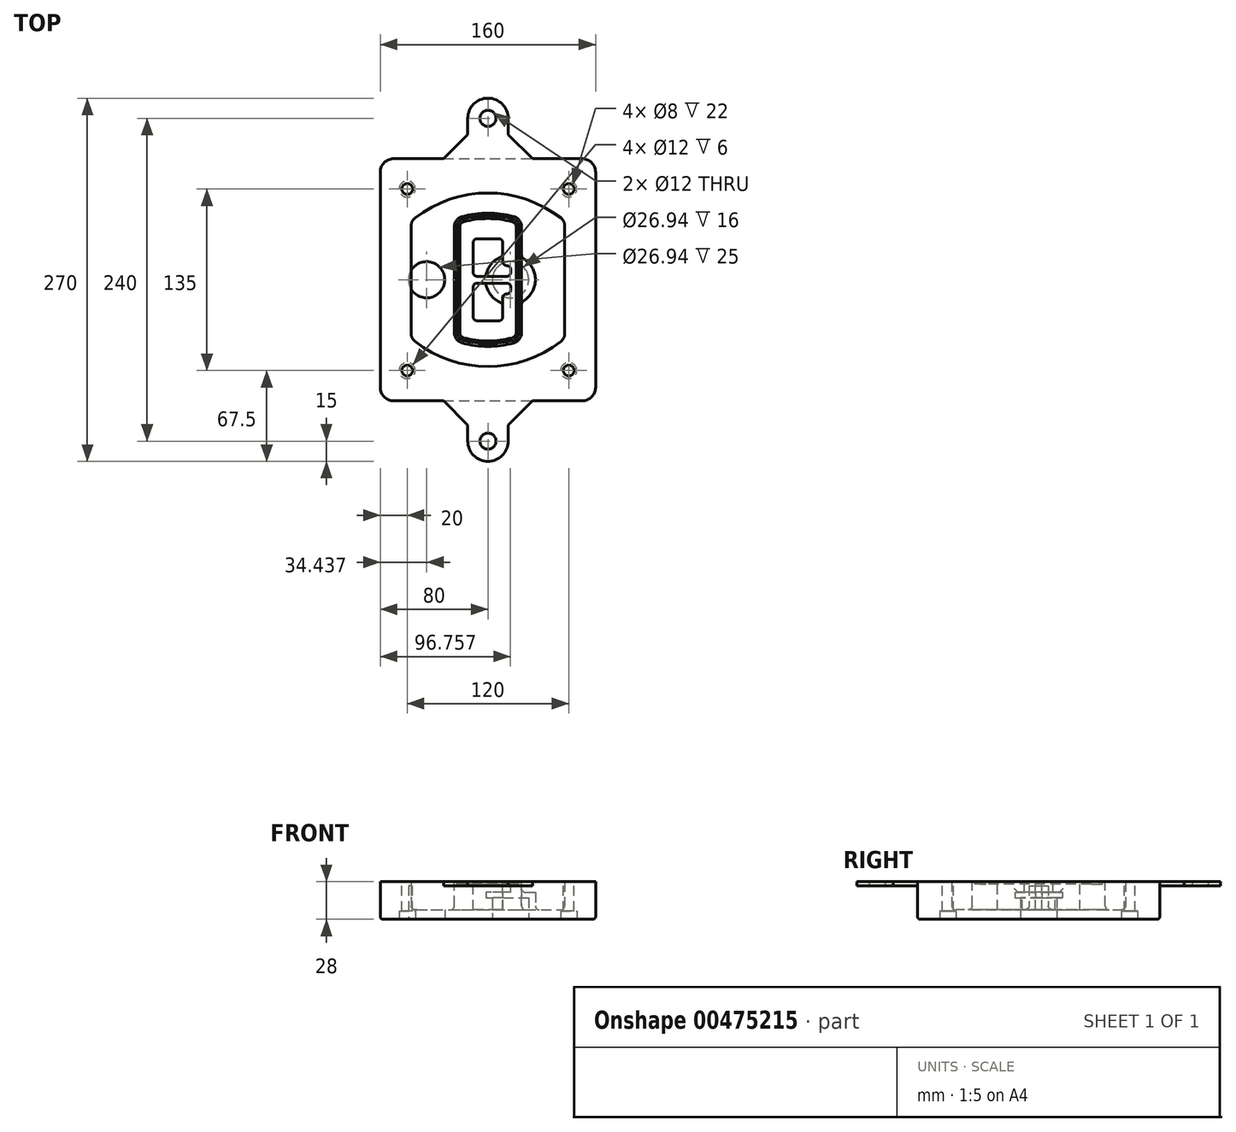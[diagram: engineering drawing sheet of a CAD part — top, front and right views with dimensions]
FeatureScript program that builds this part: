
annotation { "Feature Type Name" : "Feature", "Feature Type Description" : "" }
export const myFeature = defineFeature(function(context is Context, id is Id, definition is map)
    precondition{}
    {
        {
            var Q0;
            Q0=qCreatedBy(makeId("Top.planeOp"),FACE);
            var sketch = newSketch(context, id + "F0", { "sketchPlane" : qUnion([Q0])});
            skPoint(sketch, "E0.rect.middle", {"position": v(0, 0) * mm});
            skLineSegment(sketch, "E1.bottom", {"start": v(-70, -90) * mm, "end": v(70, -90) * mm});
            skLineSegment(sketch, "E1.top", {"start": v(-70, 90) * mm, "end": v(70, 90) * mm});
            skLineSegment(sketch, "E1.left", {"start": v(-80, -80) * mm, "end": v(-80, 80) * mm});
            skLineSegment(sketch, "E1.right", {"start": v(80, -80) * mm, "end": v(80, 80) * mm});
            skLineSegment(sketch, "E2", {"start": v(-80, 90) * mm, "end": v(80, -90) * mm, "construction": true});
            skLineSegment(sketch, "E3", {"start": v(80, 90) * mm, "end": v(-80, -90) * mm, "construction": true});
            skCircle(sketch, "E4", {"center": v(-60, 67.5) * mm, "radius": 4 * mm});
            skCircle(sketch, "E5", {"center": v(60, 67.5) * mm, "radius": 4 * mm});
            skCircle(sketch, "E6", {"center": v(60, -67.5) * mm, "radius": 4 * mm});
            skCircle(sketch, "E7", {"center": v(-60, -67.5) * mm, "radius": 4 * mm});
            skLineSegment(sketch, "E8", {"start": v(-60, 67.5) * mm, "end": v(60, 67.5) * mm, "construction": true});
            skLineSegment(sketch, "E9", {"start": v(60, 67.5) * mm, "end": v(60, -67.5) * mm, "construction": true});
            skLineSegment(sketch, "E10", {"start": v(60, -67.5) * mm, "end": v(-60, -67.5) * mm, "construction": true});
            skLineSegment(sketch, "E11", {"start": v(-60, -67.5) * mm, "end": v(-60, 67.5) * mm, "construction": true});
            skLineSegment(sketch, "E12", {"start": v(-60, 40.3) * mm, "end": v(-60, -40.3) * mm});
            skLineSegment(sketch, "E13", {"start": v(60, 40.3) * mm, "end": v(60, -40.3) * mm});
            skArc(sketch, "E14", {"start": v(56.15, 48.18) * mm, "mid": v(0, 67.5) * mm, "end": v(-56.15, 48.18) * mm});
            skArc(sketch, "E15", {"start": v(-56.15, -48.18) * mm, "mid": v(0, -67.5) * mm, "end": v(56.15, -48.18) * mm});
            skLineSegment(sketch, "E16", {"start": v(-60, 0) * mm, "end": v(60, 0) * mm, "construction": true});
            skPoint(sketch, "E17.visualSharp", {"position": v(-60, -45) * mm});
            skArc(sketch, "E17.filletArc", {"start": v(-60, -40.3) * mm, "mid": v(-58.99, -44.68) * mm, "end": v(-56.15, -48.18) * mm});
            skPoint(sketch, "E18.visualSharp", {"position": v(-60, 45) * mm});
            skArc(sketch, "E18.filletArc", {"start": v(-56.15, 48.18) * mm, "mid": v(-58.99, 44.68) * mm, "end": v(-60, 40.3) * mm});
            skPoint(sketch, "E19.visualSharp", {"position": v(60, 45) * mm});
            skArc(sketch, "E19.filletArc", {"start": v(60, 40.3) * mm, "mid": v(58.99, 44.68) * mm, "end": v(56.15, 48.18) * mm});
            skPoint(sketch, "E20.visualSharp", {"position": v(60, -45) * mm});
            skArc(sketch, "E20.filletArc", {"start": v(56.15, -48.18) * mm, "mid": v(58.99, -44.68) * mm, "end": v(60, -40.3) * mm});
            skPoint(sketch, "E21.visualSharp", {"position": v(-80, 90) * mm});
            skArc(sketch, "E21.filletArc", {"start": v(-70, 90) * mm, "mid": v(-77.07, 87.07) * mm, "end": v(-80, 80) * mm});
            skPoint(sketch, "E22.visualSharp", {"position": v(80, 90) * mm});
            skArc(sketch, "E22.filletArc", {"start": v(80, 80) * mm, "mid": v(77.07, 87.07) * mm, "end": v(70, 90) * mm});
            skPoint(sketch, "E23.visualSharp", {"position": v(80, -90) * mm});
            skArc(sketch, "E23.filletArc", {"start": v(70, -90) * mm, "mid": v(77.07, -87.07) * mm, "end": v(80, -80) * mm});
            skPoint(sketch, "E24.visualSharp", {"position": v(-80, -90) * mm});
            skArc(sketch, "E24.filletArc", {"start": v(-80, -80) * mm, "mid": v(-77.07, -87.07) * mm, "end": v(-70, -90) * mm});
            skArc(sketch, "E25.0", {"start": v(57, 40.3) * mm, "mid": v(56.3, 43.36) * mm, "end": v(54.3, 45.81) * mm});
            skLineSegment(sketch, "E25.1", {"start": v(57, 40.3) * mm, "end": v(57, -40.3) * mm});
            skArc(sketch, "E25.2", {"start": v(54.3, -45.81) * mm, "mid": v(56.3, -43.36) * mm, "end": v(57, -40.3) * mm});
            skArc(sketch, "E25.3", {"start": v(-54.3, -45.81) * mm, "mid": v(0, -64.5) * mm, "end": v(54.3, -45.81) * mm});
            skArc(sketch, "E25.4", {"start": v(-57, -40.3) * mm, "mid": v(-56.3, -43.36) * mm, "end": v(-54.3, -45.81) * mm});
            skArc(sketch, "E25.5", {"start": v(54.3, 45.81) * mm, "mid": v(0, 64.5) * mm, "end": v(-54.3, 45.81) * mm});
            skLineSegment(sketch, "E25.6", {"start": v(-57, 40.3) * mm, "end": v(-57, -40.3) * mm});
            skArc(sketch, "E25.7", {"start": v(-54.3, 45.81) * mm, "mid": v(-56.3, 43.36) * mm, "end": v(-57, 40.3) * mm});
            skArc(sketch, "E26.0", {"start": v(-58.62, 51.33) * mm, "mid": v(-62.58, 46.43) * mm, "end": v(-64, 40.3) * mm});
            skArc(sketch, "E26.1", {"start": v(58.62, 51.33) * mm, "mid": v(0, 71.5) * mm, "end": v(-58.62, 51.33) * mm});
            skArc(sketch, "E26.2", {"start": v(64, 40.3) * mm, "mid": v(62.58, 46.43) * mm, "end": v(58.62, 51.33) * mm});
            skLineSegment(sketch, "E26.3", {"start": v(64, 40.3) * mm, "end": v(64, -40.3) * mm});
            skArc(sketch, "E26.4", {"start": v(58.62, -51.33) * mm, "mid": v(62.58, -46.43) * mm, "end": v(64, -40.3) * mm});
            skLineSegment(sketch, "E26.5", {"start": v(-64, 40.3) * mm, "end": v(-64, -40.3) * mm});
            skArc(sketch, "E26.6", {"start": v(-58.62, -51.33) * mm, "mid": v(0, -71.5) * mm, "end": v(58.62, -51.33) * mm});
            skArc(sketch, "E26.7", {"start": v(-64, -40.3) * mm, "mid": v(-62.58, -46.43) * mm, "end": v(-58.62, -51.33) * mm});
            skSolve(sketch);
        }
        {
            var Q0;
            Q0=makeQuery(id+"F0.imprint","IMPRINT",FACE,{"disambiguationData":[TD([[makeQuery(id+"F0.imprint","IMPRINT",EDGE,{"derivedFrom":sQuery(id+"F0.wireOp",EDGE,"E1.bottom")}),1.0]])]});
            var Q1;
            Q1=makeQuery(id+"F0.imprint","IMPRINT",FACE,{"disambiguationData":[TD([[makeQuery(id+"F0.imprint","IMPRINT",EDGE,{"derivedFrom":sQuery(id+"F0.wireOp",EDGE,"E12")}),1.0]])]});
            var Q2;
            Q2=makeQuery(id+"F0.imprint","IMPRINT",FACE,{"disambiguationData":[TD([[makeQuery(id+"F0.imprint","IMPRINT",EDGE,{"derivedFrom":sQuery(id+"F0.wireOp",EDGE,"E25.0")}),1.0]])]});
            var Q3;
            Q3=makeQuery(id+"F0.imprint","IMPRINT",FACE,{"disambiguationData":[TD([[makeQuery(id+"F0.imprint","IMPRINT",EDGE,{"derivedFrom":sQuery(id+"F0.wireOp",EDGE,"E12")}),-1.0]])]});
            extrude(context, id + "F1", {"entities" : qUnion([Q0, Q1, Q2, Q3]), "oppositeDirection" : true, "depth" : 25 * mm});
        }
        {
            var Q0;
            Q0=makeQuery(id+"F0.imprint","IMPRINT",FACE,{"disambiguationData":[TD([[makeQuery(id+"F0.imprint","IMPRINT",EDGE,{"derivedFrom":sQuery(id+"F0.wireOp",EDGE,"E12")}),1.0]])]});
            extrude(context, id + "F2", {"entities" : qUnion([Q0]), "operationType" : NewBodyOperationType.ADD, "depth" : 3 * mm});
        }
        {
            var Q0;
            Q0=makeQuery(id+"F0.imprint","IMPRINT",FACE,{"disambiguationData":[TD([[makeQuery(id+"F0.imprint","IMPRINT",EDGE,{"derivedFrom":sQuery(id+"F0.wireOp",EDGE,"E25.0")}),1.0]])]});
            extrude(context, id + "F3", {"entities" : qUnion([Q0]), "operationType" : NewBodyOperationType.REMOVE, "oppositeDirection" : true, "depth" : 18 * mm});
        }
        {
            var Q0;
            Q0=makeQuery(id+"F2.opExtrude","CAP_FACE",FACE,{"disambiguationData":[OSD([sQuery(id+"F0.wireOp",EDGE,"E12"),sQuery(id+"F0.wireOp",EDGE,"E13"),sQuery(id+"F0.wireOp",EDGE,"E14"),sQuery(id+"F0.wireOp",EDGE,"E15"),sQuery(id+"F0.wireOp",EDGE,"E17.filletArc"),sQuery(id+"F0.wireOp",EDGE,"E18.filletArc"),sQuery(id+"F0.wireOp",EDGE,"E19.filletArc"),sQuery(id+"F0.wireOp",EDGE,"E20.filletArc"),sQuery(id+"F0.wireOp",EDGE,"E25.0"),sQuery(id+"F0.wireOp",EDGE,"E25.1"),sQuery(id+"F0.wireOp",EDGE,"E25.2"),sQuery(id+"F0.wireOp",EDGE,"E25.3"),sQuery(id+"F0.wireOp",EDGE,"E25.4"),sQuery(id+"F0.wireOp",EDGE,"E25.5"),sQuery(id+"F0.wireOp",EDGE,"E25.6"),sQuery(id+"F0.wireOp",EDGE,"E25.7")])],"isStart":false});
            var sketch = newSketch(context, id + "F4", { "sketchPlane" : qUnion([Q0])});
            skArc(sketch, "E27.0", {"start": v(-19.08, -46.97) * mm, "mid": v(0, -49.5) * mm, "end": v(19.08, -46.97) * mm});
            skArc(sketch, "E28.0", {"start": v(19.08, 46.97) * mm, "mid": v(0, 49.5) * mm, "end": v(-19.08, 46.97) * mm});
            skLineSegment(sketch, "E29", {"start": v(-25, 39.25) * mm, "end": v(-25, -39.25) * mm});
            skLineSegment(sketch, "E30", {"start": v(25, 39.25) * mm, "end": v(25, -39.25) * mm});
            skLineSegment(sketch, "E31", {"start": v(-25, 45.1) * mm, "end": v(25, 45.1) * mm, "construction": true});
            skLineSegment(sketch, "E32", {"start": v(-25, -45.1) * mm, "end": v(25, -45.1) * mm, "construction": true});
            skPoint(sketch, "E33.visualSharp", {"position": v(-25, 45.1) * mm});
            skArc(sketch, "E33.filletArc", {"start": v(-19.08, 46.97) * mm, "mid": v(-23.35, 44.11) * mm, "end": v(-25, 39.25) * mm});
            skPoint(sketch, "E34.visualSharp", {"position": v(25, 45.1) * mm});
            skArc(sketch, "E34.filletArc", {"start": v(25, 39.25) * mm, "mid": v(23.35, 44.11) * mm, "end": v(19.08, 46.97) * mm});
            skPoint(sketch, "E35.visualSharp", {"position": v(25, -45.1) * mm});
            skArc(sketch, "E35.filletArc", {"start": v(19.08, -46.97) * mm, "mid": v(23.35, -44.11) * mm, "end": v(25, -39.25) * mm});
            skPoint(sketch, "E36.visualSharp", {"position": v(-25, -45.1) * mm});
            skArc(sketch, "E36.filletArc", {"start": v(-25, -39.25) * mm, "mid": v(-23.35, -44.11) * mm, "end": v(-19.08, -46.97) * mm});
            skArc(sketch, "E37.0", {"start": v(54.3, 45.81) * mm, "mid": v(0, 64.5) * mm, "end": v(-54.3, 45.81) * mm});
            skArc(sketch, "E37.1", {"start": v(-54.3, 45.81) * mm, "mid": v(-56.3, 43.36) * mm, "end": v(-57, 40.3) * mm});
            skLineSegment(sketch, "E37.2", {"start": v(-57, 40.3) * mm, "end": v(-57, -40.3) * mm});
            skArc(sketch, "E37.3", {"start": v(-57, -40.3) * mm, "mid": v(-56.3, -43.36) * mm, "end": v(-54.3, -45.81) * mm});
            skArc(sketch, "E37.4", {"start": v(-54.3, -45.81) * mm, "mid": v(0, -64.5) * mm, "end": v(54.3, -45.81) * mm});
            skArc(sketch, "E37.5", {"start": v(54.3, -45.81) * mm, "mid": v(56.3, -43.36) * mm, "end": v(57, -40.3) * mm});
            skLineSegment(sketch, "E37.6", {"start": v(57, 40.3) * mm, "end": v(57, -40.3) * mm});
            skArc(sketch, "E37.7", {"start": v(57, 40.3) * mm, "mid": v(56.3, 43.36) * mm, "end": v(54.3, 45.81) * mm});
            skLineSegment(sketch, "E38.0", {"start": v(23, 39.25) * mm, "end": v(23, -39.25) * mm});
            skArc(sketch, "E38.1", {"start": v(18.56, -45.04) * mm, "mid": v(21.76, -42.9) * mm, "end": v(23, -39.25) * mm});
            skArc(sketch, "E38.2", {"start": v(-18.56, -45.04) * mm, "mid": v(0, -47.5) * mm, "end": v(18.56, -45.04) * mm});
            skArc(sketch, "E38.3", {"start": v(-23, -39.25) * mm, "mid": v(-21.76, -42.9) * mm, "end": v(-18.56, -45.04) * mm});
            skLineSegment(sketch, "E38.4", {"start": v(-23, 39.25) * mm, "end": v(-23, -39.25) * mm});
            skArc(sketch, "E38.5", {"start": v(23, 39.25) * mm, "mid": v(21.76, 42.9) * mm, "end": v(18.56, 45.04) * mm});
            skArc(sketch, "E38.6", {"start": v(-18.56, 45.04) * mm, "mid": v(-21.76, 42.9) * mm, "end": v(-23, 39.25) * mm});
            skArc(sketch, "E38.7", {"start": v(18.56, 45.04) * mm, "mid": v(0, 47.5) * mm, "end": v(-18.56, 45.04) * mm});
            skArc(sketch, "E39.0", {"start": v(21, 39.25) * mm, "mid": v(20.18, 41.68) * mm, "end": v(18.04, 43.1) * mm});
            skLineSegment(sketch, "E39.1", {"start": v(21, 39.25) * mm, "end": v(21, -39.25) * mm});
            skArc(sketch, "E39.2", {"start": v(18.04, -43.1) * mm, "mid": v(20.18, -41.68) * mm, "end": v(21, -39.25) * mm});
            skArc(sketch, "E39.3", {"start": v(-18.04, -43.1) * mm, "mid": v(0, -45.5) * mm, "end": v(18.04, -43.1) * mm});
            skArc(sketch, "E39.4", {"start": v(-21, -39.25) * mm, "mid": v(-20.18, -41.68) * mm, "end": v(-18.04, -43.1) * mm});
            skArc(sketch, "E39.5", {"start": v(18.04, 43.1) * mm, "mid": v(0, 45.5) * mm, "end": v(-18.04, 43.1) * mm});
            skLineSegment(sketch, "E39.6", {"start": v(-21, 39.25) * mm, "end": v(-21, -39.25) * mm});
            skArc(sketch, "E39.7", {"start": v(-18.04, 43.1) * mm, "mid": v(-20.18, 41.68) * mm, "end": v(-21, 39.25) * mm});
            skLineSegment(sketch, "E40", {"start": v(-25, 0) * mm, "end": v(25, 0) * mm, "construction": true});
            skLineSegment(sketch, "E41", {"start": v(-11, 5.5) * mm, "end": v(-11, 27.5) * mm});
            skLineSegment(sketch, "E42", {"start": v(-8, 30.5) * mm, "end": v(8, 30.5) * mm});
            skLineSegment(sketch, "E43", {"start": v(11, 27.5) * mm, "end": v(11, 13.5) * mm});
            skLineSegment(sketch, "E44", {"start": v(14, 10.5) * mm, "end": v(14, 10.5) * mm});
            skLineSegment(sketch, "E45", {"start": v(17, 7.5) * mm, "end": v(17, 5.5) * mm});
            skLineSegment(sketch, "E46", {"start": v(14, 2.5) * mm, "end": v(-8, 2.5) * mm});
            skPoint(sketch, "E47.visualSharp", {"position": v(-11, 30.5) * mm});
            skArc(sketch, "E47.filletArc", {"start": v(-8, 30.5) * mm, "mid": v(-10.12, 29.62) * mm, "end": v(-11, 27.5) * mm});
            skPoint(sketch, "E48.visualSharp", {"position": v(11, 30.5) * mm});
            skArc(sketch, "E48.filletArc", {"start": v(11, 27.5) * mm, "mid": v(10.12, 29.62) * mm, "end": v(8, 30.5) * mm});
            skPoint(sketch, "E49.visualSharp", {"position": v(11, 10.5) * mm});
            skArc(sketch, "E49.filletArc", {"start": v(11, 13.5) * mm, "mid": v(11.88, 11.38) * mm, "end": v(14, 10.5) * mm});
            skPoint(sketch, "E50.visualSharp", {"position": v(17, 10.5) * mm});
            skArc(sketch, "E50.filletArc", {"start": v(17, 7.5) * mm, "mid": v(16.12, 9.62) * mm, "end": v(14, 10.5) * mm});
            skPoint(sketch, "E51.visualSharp", {"position": v(17, 2.5) * mm});
            skArc(sketch, "E51.filletArc", {"start": v(14, 2.5) * mm, "mid": v(16.12, 3.38) * mm, "end": v(17, 5.5) * mm});
            skPoint(sketch, "E52.visualSharp", {"position": v(-11, 2.5) * mm});
            skArc(sketch, "E52.filletArc", {"start": v(-11, 5.5) * mm, "mid": v(-10.12, 3.38) * mm, "end": v(-8, 2.5) * mm});
            skLineSegment(sketch, "E53.0.MirrorCS", {"start": v(14, -2.5) * mm, "end": v(-8, -2.5) * mm});
            skArc(sketch, "E54.0.MirrorCS", {"start": v(-11, -5.5) * mm, "mid": v(-10.12, -3.38) * mm, "end": v(-8, -2.5) * mm});
            skLineSegment(sketch, "E55.0.MirrorCS", {"start": v(-11, -5.5) * mm, "end": v(-11, -27.5) * mm});
            skArc(sketch, "E56.0.MirrorCS", {"start": v(-8, -30.5) * mm, "mid": v(-10.12, -29.62) * mm, "end": v(-11, -27.5) * mm});
            skLineSegment(sketch, "E57.0.MirrorCS", {"start": v(-8, -30.5) * mm, "end": v(8, -30.5) * mm});
            skArc(sketch, "E58.0.MirrorCS", {"start": v(11, -27.5) * mm, "mid": v(10.12, -29.62) * mm, "end": v(8, -30.5) * mm});
            skLineSegment(sketch, "E59.0.MirrorCS", {"start": v(11, -27.5) * mm, "end": v(11, -13.5) * mm});
            skArc(sketch, "E60.0.MirrorCS", {"start": v(11, -13.5) * mm, "mid": v(11.88, -11.38) * mm, "end": v(14, -10.5) * mm});
            skArc(sketch, "E61.0.MirrorCS", {"start": v(17, -7.5) * mm, "mid": v(16.12, -9.62) * mm, "end": v(14, -10.5) * mm});
            skLineSegment(sketch, "E62.0.MirrorCS", {"start": v(17, -7.5) * mm, "end": v(17, -5.5) * mm});
            skArc(sketch, "E63.0.MirrorCS", {"start": v(14, -2.5) * mm, "mid": v(16.12, -3.38) * mm, "end": v(17, -5.5) * mm});
            skSolve(sketch);
        }
        {
            var Q0;
            Q0=makeQuery(id+"F4.imprint","IMPRINT",FACE,{"disambiguationData":[TD([[makeQuery(id+"F4.imprint","IMPRINT",EDGE,{"derivedFrom":sQuery(id+"F4.wireOp",EDGE,"E27.0")}),1.0]])]});
            var Q1;
            Q1=makeQuery(id+"F4.imprint","IMPRINT",FACE,{"disambiguationData":[TD([[makeQuery(id+"F4.imprint","IMPRINT",EDGE,{"derivedFrom":sQuery(id+"F4.wireOp",EDGE,"E38.0")}),-1.0]])]});
            var Q2;
            Q2=makeQuery(id+"F4.imprint","IMPRINT",FACE,{"disambiguationData":[TD([[makeQuery(id+"F4.imprint","IMPRINT",EDGE,{"derivedFrom":sQuery(id+"F4.wireOp",EDGE,"E39.0")}),1.0]])]});
            extrude(context, id + "F5", {"entities" : qUnion([Q0, Q1, Q2]), "operationType" : NewBodyOperationType.ADD, "endBound" : BoundingType.UP_TO_NEXT, "oppositeDirection" : true, "depth" : 25 * mm});
        }
        {
            var Q0;
            Q0=makeQuery(id+"F4.imprint","IMPRINT",FACE,{"disambiguationData":[TD([[makeQuery(id+"F4.imprint","IMPRINT",EDGE,{"derivedFrom":sQuery(id+"F4.wireOp",EDGE,"E38.0")}),-1.0]])]});
            extrude(context, id + "F6", {"entities" : qUnion([Q0]), "operationType" : NewBodyOperationType.REMOVE, "oppositeDirection" : true, "depth" : 2 * mm});
        }
        {
            var Q0;
            Q0=makeQuery(id+"F1.opExtrude","CAP_FACE",FACE,{"disambiguationData":[OSD([sQuery(id+"F0.wireOp",EDGE,"E1.bottom"),sQuery(id+"F0.wireOp",EDGE,"E1.top"),sQuery(id+"F0.wireOp",EDGE,"E1.left"),sQuery(id+"F0.wireOp",EDGE,"E1.right"),sQuery(id+"F0.wireOp",EDGE,"E4"),sQuery(id+"F0.wireOp",EDGE,"E5"),sQuery(id+"F0.wireOp",EDGE,"E6"),sQuery(id+"F0.wireOp",EDGE,"E7"),sQuery(id+"F0.wireOp",EDGE,"E21.filletArc"),sQuery(id+"F0.wireOp",EDGE,"E22.filletArc"),sQuery(id+"F0.wireOp",EDGE,"E23.filletArc"),sQuery(id+"F0.wireOp",EDGE,"E24.filletArc")])],"isStart":false});
            var sketch = newSketch(context, id + "F7", { "sketchPlane" : qUnion([Q0])});
            skCircle(sketch, "E64", {"center": v(16.76, 0) * mm, "radius": 13.47 * mm});
            skCircle(sketch, "E65", {"center": v(-45.56, 0) * mm, "radius": 13.47 * mm});
            skLineSegment(sketch, "E66", {"start": v(80, 0) * mm, "end": v(-80, 0) * mm});
            skCircle(sketch, "E67", {"center": v(16.76, 0) * mm, "radius": 18.47 * mm});
            skCircle(sketch, "E68", {"center": v(60, -67.5) * mm, "radius": 6 * mm});
            skCircle(sketch, "E69", {"center": v(-60, -67.5) * mm, "radius": 6 * mm});
            skCircle(sketch, "E70", {"center": v(-60, 67.5) * mm, "radius": 6 * mm});
            skCircle(sketch, "E71", {"center": v(60, 67.5) * mm, "radius": 6 * mm});
            skSolve(sketch);
        }
        {
            var Q0;
            {var subQ1=sQuery(id+"F7.wireOp",EDGE,"E66");var subQ4=sQuery(id+"F7.wireOp",EDGE,"E64");var subQ6=makeQuery(id+"F7.imprint","INTERSECT",VERTEX,{"disambiguationData":[OD(0.0)],"derivedFrom":[subQ4,subQ1]});Q0=makeQuery(id+"F7.imprint","IMPRINT",FACE,{"disambiguationData":[TD([[makeQuery(id+"F7.imprint","IMPRINT",EDGE,{"disambiguationData":[TD([[subQ6,-1.0]])],"derivedFrom":subQ4}),-1.0]])]});}
            var Q1;
            {var subQ0=sQuery(id+"F7.wireOp",EDGE,"E66");var subQ1=sQuery(id+"F7.wireOp",EDGE,"E64");var subQ3=makeQuery(id+"F7.imprint","INTERSECT",VERTEX,{"disambiguationData":[OD(0.0)],"derivedFrom":[subQ1,subQ0]});Q1=makeQuery(id+"F7.imprint","IMPRINT",FACE,{"disambiguationData":[TD([[makeQuery(id+"F7.imprint","IMPRINT",EDGE,{"disambiguationData":[TD([[subQ3,-1.0]])],"derivedFrom":subQ1}),1.0]])]});}
            var Q2;
            {var subQ0=sQuery(id+"F7.wireOp",EDGE,"E66");var subQ1=sQuery(id+"F7.wireOp",EDGE,"E64");var subQ3=makeQuery(id+"F7.imprint","INTERSECT",VERTEX,{"disambiguationData":[OD(0.0)],"derivedFrom":[subQ1,subQ0]});Q2=makeQuery(id+"F7.imprint","IMPRINT",FACE,{"disambiguationData":[TD([[makeQuery(id+"F7.imprint","IMPRINT",EDGE,{"disambiguationData":[TD([[subQ3,1.0]])],"derivedFrom":subQ1}),1.0]])]});}
            var Q3;
            {var subQ1=sQuery(id+"F7.wireOp",EDGE,"E66");var subQ4=sQuery(id+"F7.wireOp",EDGE,"E64");var subQ6=makeQuery(id+"F7.imprint","INTERSECT",VERTEX,{"disambiguationData":[OD(0.0)],"derivedFrom":[subQ4,subQ1]});Q3=makeQuery(id+"F7.imprint","IMPRINT",FACE,{"disambiguationData":[TD([[makeQuery(id+"F7.imprint","IMPRINT",EDGE,{"disambiguationData":[TD([[subQ6,1.0]])],"derivedFrom":subQ4}),-1.0]])]});}
            extrude(context, id + "F8", {"entities" : qUnion([Q0, Q1, Q2, Q3]), "operationType" : NewBodyOperationType.ADD, "oppositeDirection" : true, "depth" : 20 * mm});
        }
        {
            var Q0;
            {var subQ0=sQuery(id+"F7.wireOp",EDGE,"E66");var subQ1=sQuery(id+"F7.wireOp",EDGE,"E64");var subQ3=makeQuery(id+"F7.imprint","INTERSECT",VERTEX,{"disambiguationData":[OD(0.0)],"derivedFrom":[subQ1,subQ0]});Q0=makeQuery(id+"F7.imprint","IMPRINT",FACE,{"disambiguationData":[TD([[makeQuery(id+"F7.imprint","IMPRINT",EDGE,{"disambiguationData":[TD([[subQ3,-1.0]])],"derivedFrom":subQ1}),1.0]])]});}
            var Q1;
            {var subQ0=sQuery(id+"F7.wireOp",EDGE,"E66");var subQ1=sQuery(id+"F7.wireOp",EDGE,"E64");var subQ3=makeQuery(id+"F7.imprint","INTERSECT",VERTEX,{"disambiguationData":[OD(0.0)],"derivedFrom":[subQ1,subQ0]});Q1=makeQuery(id+"F7.imprint","IMPRINT",FACE,{"disambiguationData":[TD([[makeQuery(id+"F7.imprint","IMPRINT",EDGE,{"disambiguationData":[TD([[subQ3,1.0]])],"derivedFrom":subQ1}),1.0]])]});}
            extrude(context, id + "F9", {"entities" : qUnion([Q0, Q1]), "operationType" : NewBodyOperationType.REMOVE, "oppositeDirection" : true, "depth" : 16 * mm});
        }
        {
            var Q0;
            {var subQ0=sQuery(id+"F7.wireOp",EDGE,"E66");var subQ1=sQuery(id+"F7.wireOp",EDGE,"E65");var subQ3=makeQuery(id+"F7.imprint","INTERSECT",VERTEX,{"disambiguationData":[OD(0.0)],"derivedFrom":[subQ1,subQ0]});Q0=makeQuery(id+"F7.imprint","IMPRINT",FACE,{"disambiguationData":[TD([[makeQuery(id+"F7.imprint","IMPRINT",EDGE,{"disambiguationData":[TD([[subQ3,-1.0]])],"derivedFrom":subQ1}),1.0]])]});}
            var Q1;
            {var subQ0=sQuery(id+"F7.wireOp",EDGE,"E66");var subQ1=sQuery(id+"F7.wireOp",EDGE,"E65");var subQ3=makeQuery(id+"F7.imprint","INTERSECT",VERTEX,{"disambiguationData":[OD(0.0)],"derivedFrom":[subQ1,subQ0]});Q1=makeQuery(id+"F7.imprint","IMPRINT",FACE,{"disambiguationData":[TD([[makeQuery(id+"F7.imprint","IMPRINT",EDGE,{"disambiguationData":[TD([[subQ3,1.0]])],"derivedFrom":subQ1}),1.0]])]});}
            extrude(context, id + "F10", {"entities" : qUnion([Q0, Q1]), "operationType" : NewBodyOperationType.REMOVE, "oppositeDirection" : true, "depth" : 25 * mm});
        }
        {
            var Q0;
            Q0=makeQuery(id+"F7.imprint","IMPRINT",FACE,{"disambiguationData":[TD([[makeQuery(id+"F7.imprint","IMPRINT",EDGE,{"derivedFrom":sQuery(id+"F7.wireOp",EDGE,"E68")}),1.0]])]});
            var Q1;
            Q1=makeQuery(id+"F7.imprint","IMPRINT",FACE,{"disambiguationData":[TD([[makeQuery(id+"F7.imprint","IMPRINT",EDGE,{"derivedFrom":makeQuery(id+"F1.opExtrude","CAP_EDGE",EDGE,{"disambiguationData":[OSD([sQuery(id+"F0.wireOp",EDGE,"E5")])],"isStart":false})}),-1.0]])]});
            var Q2;
            Q2=makeQuery(id+"F7.imprint","IMPRINT",FACE,{"disambiguationData":[TD([[makeQuery(id+"F7.imprint","IMPRINT",EDGE,{"derivedFrom":sQuery(id+"F7.wireOp",EDGE,"E69")}),1.0]])]});
            var Q3;
            Q3=makeQuery(id+"F7.imprint","IMPRINT",FACE,{"disambiguationData":[TD([[makeQuery(id+"F7.imprint","IMPRINT",EDGE,{"derivedFrom":makeQuery(id+"F1.opExtrude","CAP_EDGE",EDGE,{"disambiguationData":[OSD([sQuery(id+"F0.wireOp",EDGE,"E4")])],"isStart":false})}),-1.0]])]});
            var Q4;
            Q4=makeQuery(id+"F7.imprint","IMPRINT",FACE,{"disambiguationData":[TD([[makeQuery(id+"F7.imprint","IMPRINT",EDGE,{"derivedFrom":sQuery(id+"F7.wireOp",EDGE,"E70")}),1.0]])]});
            var Q5;
            Q5=makeQuery(id+"F7.imprint","IMPRINT",FACE,{"disambiguationData":[TD([[makeQuery(id+"F7.imprint","IMPRINT",EDGE,{"derivedFrom":makeQuery(id+"F1.opExtrude","CAP_EDGE",EDGE,{"disambiguationData":[OSD([sQuery(id+"F0.wireOp",EDGE,"E7")])],"isStart":false})}),-1.0]])]});
            var Q6;
            Q6=makeQuery(id+"F7.imprint","IMPRINT",FACE,{"disambiguationData":[TD([[makeQuery(id+"F7.imprint","IMPRINT",EDGE,{"derivedFrom":sQuery(id+"F7.wireOp",EDGE,"E71")}),1.0]])]});
            var Q7;
            Q7=makeQuery(id+"F7.imprint","IMPRINT",FACE,{"disambiguationData":[TD([[makeQuery(id+"F7.imprint","IMPRINT",EDGE,{"derivedFrom":makeQuery(id+"F1.opExtrude","CAP_EDGE",EDGE,{"disambiguationData":[OSD([sQuery(id+"F0.wireOp",EDGE,"E6")])],"isStart":false})}),-1.0]])]});
            extrude(context, id + "F11", {"entities" : qUnion([Q0, Q1, Q2, Q3, Q4, Q5, Q6, Q7]), "operationType" : NewBodyOperationType.REMOVE, "oppositeDirection" : true, "depth" : 6 * mm});
        }
        {
            var Q0;
            Q0=makeQuery(id+"F9.boolean.opBoolean","COPY",FACE,{"derivedFrom":makeQuery(id+"F9.opExtrude","CAP_FACE",FACE,{"disambiguationData":[OSD([sQuery(id+"F7.wireOp",EDGE,"E64")])],"isStart":false})});
            var sketch = newSketch(context, id + "F12", { "sketchPlane" : qUnion([Q0])});
            skArc(sketch, "E72.0", {"start": v(11, 17.55) * mm, "mid": v(2.57, 11.82) * mm, "end": v(-1.54, 2.5) * mm});
            skArc(sketch, "E72.1", {"start": v(-1.54, -2.5) * mm, "mid": v(2.57, -11.82) * mm, "end": v(11, -17.55) * mm});
            skLineSegment(sketch, "E73", {"start": v(-1.54, -2.5) * mm, "end": v(14, -2.5) * mm});
            skLineSegment(sketch, "E74.0", {"start": v(14, 2.5) * mm, "end": v(-1.54, 2.5) * mm});
            skArc(sketch, "E74.1", {"start": v(14, 2.5) * mm, "mid": v(16.12, 3.38) * mm, "end": v(17, 5.5) * mm});
            skLineSegment(sketch, "E74.2", {"start": v(17, 7.5) * mm, "end": v(17, 5.5) * mm});
            skArc(sketch, "E74.3", {"start": v(17, 7.5) * mm, "mid": v(16.12, 9.62) * mm, "end": v(14, 10.5) * mm});
            skArc(sketch, "E74.4", {"start": v(11, 13.5) * mm, "mid": v(11.88, 11.38) * mm, "end": v(14, 10.5) * mm});
            skLineSegment(sketch, "E74.5", {"start": v(11, 17.55) * mm, "end": v(11, 13.5) * mm});
            skLineSegment(sketch, "E74.7", {"start": v(14, -2.5) * mm, "end": v(-1.54, -2.5) * mm});
            skArc(sketch, "E74.8", {"start": v(14, -2.5) * mm, "mid": v(16.12, -3.38) * mm, "end": v(17, -5.5) * mm});
            skLineSegment(sketch, "E74.9", {"start": v(17, -7.5) * mm, "end": v(17, -5.5) * mm});
            skArc(sketch, "E74.10", {"start": v(17, -7.5) * mm, "mid": v(16.12, -9.62) * mm, "end": v(14, -10.5) * mm});
            skArc(sketch, "E74.11", {"start": v(11, -13.5) * mm, "mid": v(11.88, -11.38) * mm, "end": v(14, -10.5) * mm});
            skLineSegment(sketch, "E74.12", {"start": v(11, -17.55) * mm, "end": v(11, -13.5) * mm});
            skPoint(sketch, "E75.orphan", {"position": v(11, -27.5) * mm});
            skPoint(sketch, "E76.orphan", {"position": v(-8, -2.5) * mm});
            skPoint(sketch, "E77.orphan", {"position": v(-8, 2.5) * mm});
            skPoint(sketch, "E78.orphan", {"position": v(11, 27.5) * mm});
            skSolve(sketch);
        }
        {
            var Q0;
            {var subQ7=sQuery(id+"F12.wireOp",EDGE,"E72.0");var subQ14=sQuery(id+"F12.wireOp",EDGE,"E72.1");var subQ16=sQuery(id+"F12.wireOp",EDGE,"E74.1");var subQ18=sQuery(id+"F12.wireOp",EDGE,"E74.8");Q0=qUnion([makeQuery(id+"F12.imprint","IMPRINT",FACE,{"disambiguationData":[TD([[makeQuery(id+"F12.imprint","IMPRINT",EDGE,{"derivedFrom":subQ7}),1.0]])]}),makeQuery(id+"F12.imprint","IMPRINT",FACE,{"disambiguationData":[TD([[makeQuery(id+"F12.imprint","IMPRINT",EDGE,{"derivedFrom":subQ14}),1.0]])]}),makeQuery(id+"F12.imprint","IMPRINT",FACE,{"disambiguationData":[TD([[makeQuery(id+"F12.imprint","IMPRINT",EDGE,{"derivedFrom":subQ16}),1.0]])]}),makeQuery(id+"F12.imprint","IMPRINT",FACE,{"disambiguationData":[TD([[makeQuery(id+"F12.imprint","IMPRINT",EDGE,{"derivedFrom":subQ18}),-1.0]])]})]);}
            var Q1;
            Q1=makeQuery(id+"F5.boolean.opBoolean","SPLIT",FACE,{"disambiguationData":[TD([makeQuery(id+"F5.opExtrude","SWEPT_FACE",FACE,{"disambiguationData":[OSD([sQuery(id+"F4.wireOp",EDGE,"E41")])]})])],"derivedFrom":makeQuery(id+"F3.boolean.opBoolean","COPY",FACE,{"derivedFrom":makeQuery(id+"F3.opExtrude","CAP_FACE",FACE,{"disambiguationData":[OSD([sQuery(id+"F0.wireOp",EDGE,"E25.0"),sQuery(id+"F0.wireOp",EDGE,"E25.1"),sQuery(id+"F0.wireOp",EDGE,"E25.2"),sQuery(id+"F0.wireOp",EDGE,"E25.3"),sQuery(id+"F0.wireOp",EDGE,"E25.4"),sQuery(id+"F0.wireOp",EDGE,"E25.5"),sQuery(id+"F0.wireOp",EDGE,"E25.6"),sQuery(id+"F0.wireOp",EDGE,"E25.7")])],"isStart":false})})});
            extrude(context, id + "F13", {"entities" : qUnion([Q0]), "operationType" : NewBodyOperationType.REMOVE, "endBound" : BoundingType.UP_TO_SURFACE, "endBoundEntityFace" : qUnion([Q1]), "depth" : 25 * mm});
        }
        {
            var Q0;
            Q0=makeQuery(id+"F3.boolean.opBoolean","COPY",EDGE,{"derivedFrom":makeQuery(id+"F3.opExtrude","CAP_EDGE",EDGE,{"disambiguationData":[OSD([sQuery(id+"F0.wireOp",EDGE,"E25.6")])],"isStart":false})});
            var Q1;
            Q1=makeQuery(id+"F8.boolean.opBoolean","INTERSECT",EDGE,{"derivedFrom":[makeQuery(id+"F5.opExtrude","SWEPT_FACE",FACE,{"disambiguationData":[OSD([sQuery(id+"F4.wireOp",EDGE,"E30")])]}),makeQuery(id+"F8.opExtrude","CAP_FACE",FACE,{"disambiguationData":[OSD([sQuery(id+"F7.wireOp",EDGE,"E67")])],"isStart":false})]});
            var Q2;
            Q2=makeQuery(id+"F8.boolean.opBoolean","INTERSECT",EDGE,{"disambiguationData":[OD(1.0)],"derivedFrom":[makeQuery(id+"F5.opExtrude","SWEPT_FACE",FACE,{"disambiguationData":[OSD([sQuery(id+"F4.wireOp",EDGE,"E30")])]}),makeQuery(id+"F8.opExtrude","SWEPT_FACE",FACE,{"disambiguationData":[OSD([sQuery(id+"F7.wireOp",EDGE,"E67")])]})]});
            var Q3;
            {var subQ0=sQuery(id+"F4.wireOp",EDGE,"E30");Q3=makeQuery(id+"F8.boolean.opBoolean","SPLIT",EDGE,{"disambiguationData":[TD([makeQuery(id+"F5.opExtrude","SWEPT_FACE",FACE,{"disambiguationData":[OSD([sQuery(id+"F4.wireOp",EDGE,"E35.filletArc")])]})])],"derivedFrom":makeQuery(id+"F5.opExtrude","CAP_EDGE",EDGE,{"disambiguationData":[OSD([subQ0])],"isStart":false})});}
            var Q4;
            {var subQ0=sQuery(id+"F0.wireOp",EDGE,"E25.7");var subQ1=sQuery(id+"F0.wireOp",EDGE,"E25.1");var subQ2=sQuery(id+"F0.wireOp",EDGE,"E25.6");var subQ3=sQuery(id+"F0.wireOp",EDGE,"E25.5");var subQ4=sQuery(id+"F0.wireOp",EDGE,"E25.4");var subQ5=sQuery(id+"F0.wireOp",EDGE,"E25.0");var subQ6=sQuery(id+"F0.wireOp",EDGE,"E25.2");var subQ7=sQuery(id+"F0.wireOp",EDGE,"E25.3");Q4=makeQuery(id+"F8.boolean.opBoolean","INTERSECT",EDGE,{"derivedFrom":[makeQuery(id+"F5.boolean.opBoolean","SPLIT",FACE,{"disambiguationData":[TD([makeQuery(id+"F2.opExtrude","SWEPT_FACE",FACE,{"disambiguationData":[OSD([subQ5])]})])],"derivedFrom":makeQuery(id+"F3.boolean.opBoolean","COPY",FACE,{"derivedFrom":makeQuery(id+"F3.opExtrude","CAP_FACE",FACE,{"disambiguationData":[OSD([subQ5,subQ1,subQ6,subQ7,subQ4,subQ3,subQ2,subQ0])],"isStart":false})})}),makeQuery(id+"F8.opExtrude","SWEPT_FACE",FACE,{"disambiguationData":[OSD([sQuery(id+"F7.wireOp",EDGE,"E67")])]})]});}
            var Q5;
            Q5=makeQuery(id+"F8.boolean.opBoolean","INTERSECT",EDGE,{"disambiguationData":[OD(0.0)],"derivedFrom":[makeQuery(id+"F5.opExtrude","SWEPT_FACE",FACE,{"disambiguationData":[OSD([sQuery(id+"F4.wireOp",EDGE,"E30")])]}),makeQuery(id+"F8.opExtrude","SWEPT_FACE",FACE,{"disambiguationData":[OSD([sQuery(id+"F7.wireOp",EDGE,"E67")])]})]});
            fillet(context, id + "F14", {"entities" : qUnion([Q0, Q1, Q2, Q3, Q4, Q5]), "radius" : 3 * mm, "tangentPropagation" : true, "allowEdgeOverflow" : false});
        }
        {
            var Q0;
            Q0=makeQuery(id+"F1.opExtrude","CAP_EDGE",EDGE,{"disambiguationData":[OSD([sQuery(id+"F0.wireOp",EDGE,"E1.bottom")])],"isStart":false});
            fillet(context, id + "F15", {"entities" : qUnion([Q0]), "radius" : 2 * mm, "tangentPropagation" : true, "allowEdgeOverflow" : false});
        }
        {
            var Q0;
            Q0=qCreatedBy(makeId("Top.planeOp"),FACE);
            var sketch = newSketch(context, id + "F16", { "sketchPlane" : qUnion([Q0])});
            skCircle(sketch, "E79.0", {"center": v(-60, -67.5) * mm, "radius": 4 * mm});
            skCircle(sketch, "E79.1", {"center": v(-60, 67.5) * mm, "radius": 4 * mm});
            skCircle(sketch, "E79.2", {"center": v(60, 67.5) * mm, "radius": 4 * mm});
            skLineSegment(sketch, "E79.3", {"start": v(-80, -80) * mm, "end": v(-80, 80) * mm});
            skArc(sketch, "E79.4", {"start": v(-70, 90) * mm, "mid": v(-77.07, 87.07) * mm, "end": v(-80, 80) * mm});
            skLineSegment(sketch, "E79.5", {"start": v(-70, 90) * mm, "end": v(70, 90) * mm});
            skArc(sketch, "E79.6", {"start": v(80, 80) * mm, "mid": v(77.07, 87.07) * mm, "end": v(70, 90) * mm});
            skLineSegment(sketch, "E79.7", {"start": v(80, -80) * mm, "end": v(80, 80) * mm});
            skArc(sketch, "E79.8", {"start": v(70, -90) * mm, "mid": v(77.07, -87.07) * mm, "end": v(80, -80) * mm});
            skLineSegment(sketch, "E79.9", {"start": v(-70, -90) * mm, "end": v(70, -90) * mm});
            skArc(sketch, "E79.10", {"start": v(-80, -80) * mm, "mid": v(-77.07, -87.07) * mm, "end": v(-70, -90) * mm});
            skArc(sketch, "E79.11", {"start": v(-56.15, -48.18) * mm, "mid": v(0, -67.5) * mm, "end": v(56.15, -48.18) * mm});
            skArc(sketch, "E79.12", {"start": v(-60, -40.3) * mm, "mid": v(-58.99, -44.68) * mm, "end": v(-56.15, -48.18) * mm});
            skLineSegment(sketch, "E79.13", {"start": v(-60, 40.3) * mm, "end": v(-60, -40.3) * mm});
            skArc(sketch, "E79.14", {"start": v(-56.15, 48.18) * mm, "mid": v(-58.99, 44.68) * mm, "end": v(-60, 40.3) * mm});
            skArc(sketch, "E79.15", {"start": v(56.15, 48.18) * mm, "mid": v(0, 67.5) * mm, "end": v(-56.15, 48.18) * mm});
            skArc(sketch, "E79.16", {"start": v(60, 40.3) * mm, "mid": v(58.99, 44.68) * mm, "end": v(56.15, 48.18) * mm});
            skLineSegment(sketch, "E79.17", {"start": v(60, 40.3) * mm, "end": v(60, -40.3) * mm});
            skArc(sketch, "E79.18", {"start": v(56.15, -48.18) * mm, "mid": v(58.99, -44.68) * mm, "end": v(60, -40.3) * mm});
            skCircle(sketch, "E80.11", {"center": v(60, -67.5) * mm, "radius": 4 * mm});
            skLineSegment(sketch, "E81", {"start": v(0, 90) * mm, "end": v(0, 120) * mm, "construction": true});
            skLineSegment(sketch, "E82", {"start": v(-33, 90) * mm, "end": v(-15, 108) * mm});
            skLineSegment(sketch, "E83", {"start": v(33, 90) * mm, "end": v(15, 108) * mm});
            skLineSegment(sketch, "E84", {"start": v(-15, 108) * mm, "end": v(-15, 120) * mm});
            skLineSegment(sketch, "E85", {"start": v(15, 108) * mm, "end": v(15, 120) * mm});
            skArc(sketch, "E86", {"start": v(-15, 120) * mm, "mid": v(0, 135) * mm, "end": v(15, 120) * mm});
            skCircle(sketch, "E87", {"center": v(0, 120) * mm, "radius": 6 * mm});
            skLineSegment(sketch, "E88", {"start": v(-80, 0) * mm, "end": v(80, 0) * mm, "construction": true});
            skLineSegment(sketch, "E89.MirrorCS", {"start": v(33, -90) * mm, "end": v(15, -108) * mm});
            skLineSegment(sketch, "E90.MirrorCS", {"start": v(-33, -90) * mm, "end": v(-15, -108) * mm});
            skLineSegment(sketch, "E91.MirrorCS", {"start": v(-15, -108) * mm, "end": v(-15, -120) * mm});
            skCircle(sketch, "E92.MirrorC", {"center": v(0, -120) * mm, "radius": 6 * mm});
            skLineSegment(sketch, "E93.MirrorCS", {"start": v(0, -90) * mm, "end": v(0, -120) * mm, "construction": true});
            skLineSegment(sketch, "E94.MirrorCS", {"start": v(15, -108) * mm, "end": v(15, -120) * mm});
            skArc(sketch, "E95.MirrorCS", {"start": v(-15, -120) * mm, "mid": v(0, -135) * mm, "end": v(15, -120) * mm});
            skSolve(sketch);
        }
        {
            var Q0;
            Q0 = qSketchRegion(id + "F16", true);
            var Q1;
            Q1=makeQuery(id+"F2.opExtrude","CAP_FACE",FACE,{"disambiguationData":[OSD([sQuery(id+"F0.wireOp",EDGE,"E12"),sQuery(id+"F0.wireOp",EDGE,"E13"),sQuery(id+"F0.wireOp",EDGE,"E14"),sQuery(id+"F0.wireOp",EDGE,"E15"),sQuery(id+"F0.wireOp",EDGE,"E17.filletArc"),sQuery(id+"F0.wireOp",EDGE,"E18.filletArc"),sQuery(id+"F0.wireOp",EDGE,"E19.filletArc"),sQuery(id+"F0.wireOp",EDGE,"E20.filletArc"),sQuery(id+"F0.wireOp",EDGE,"E25.0"),sQuery(id+"F0.wireOp",EDGE,"E25.1"),sQuery(id+"F0.wireOp",EDGE,"E25.2"),sQuery(id+"F0.wireOp",EDGE,"E25.3"),sQuery(id+"F0.wireOp",EDGE,"E25.4"),sQuery(id+"F0.wireOp",EDGE,"E25.5"),sQuery(id+"F0.wireOp",EDGE,"E25.6"),sQuery(id+"F0.wireOp",EDGE,"E25.7")])],"isStart":false});
            extrude(context, id + "F17", {"entities" : qUnion([Q0]), "operationType" : NewBodyOperationType.ADD, "endBound" : BoundingType.UP_TO_SURFACE, "endBoundEntityFace" : qUnion([Q1]), "depth" : 25 * mm});
        }
    });
